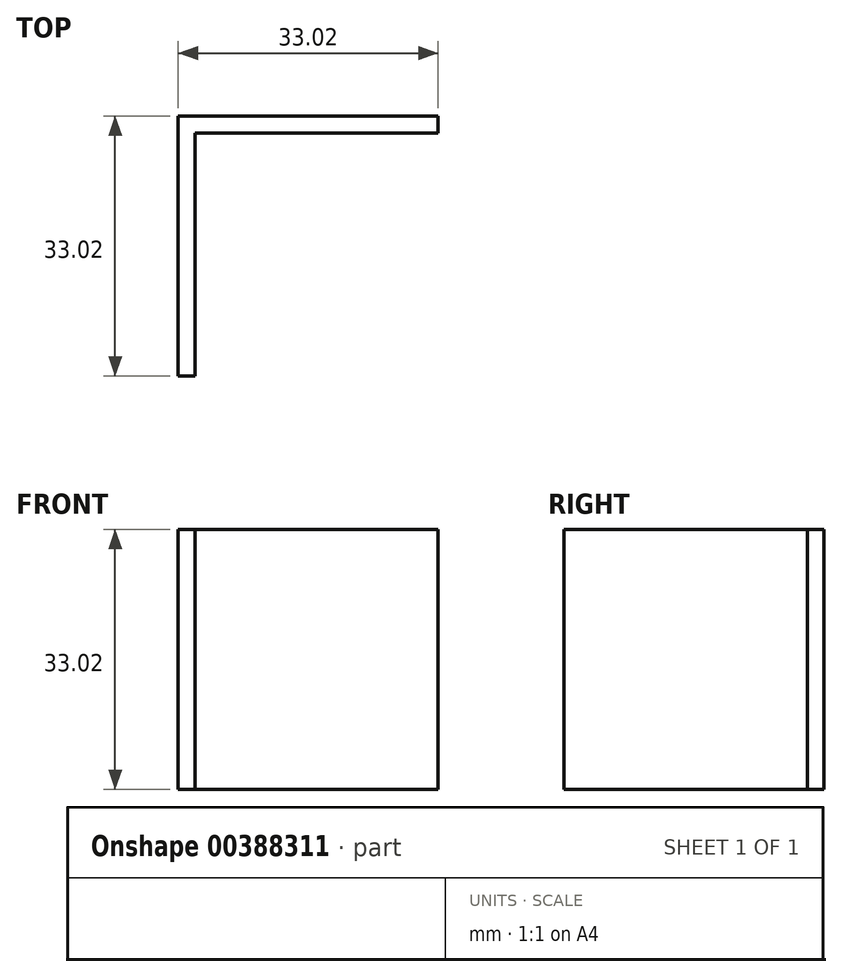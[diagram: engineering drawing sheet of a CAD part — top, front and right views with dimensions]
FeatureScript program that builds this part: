
annotation { "Feature Type Name" : "Feature", "Feature Type Description" : "" }
export const myFeature = defineFeature(function(context is Context, id is Id, definition is map)
    precondition{}
    {
        {
            var Q0;
            Q0=qCreatedBy(makeId("Front.planeOp"),FACE);
            var sketch = newSketch(context, id + "F0", { "sketchPlane" : qUnion([Q0])});
            skLineSegment(sketch, "E0", {"start": v(-20.89, 19.99) * mm, "end": v(-20.89, -13.03) * mm});
            skLineSegment(sketch, "E1", {"start": v(-20.89, -13.03) * mm, "end": v(12.13, -13.03) * mm});
            skLineSegment(sketch, "E2", {"start": v(12.13, -13.03) * mm, "end": v(12.13, 19.99) * mm});
            skLineSegment(sketch, "E3", {"start": v(12.13, 19.99) * mm, "end": v(-20.89, 19.99) * mm});
            skSolve(sketch);
        }
        {
            var Q0;
            Q0=makeQuery(id+"F0.imprint","IMPRINT",FACE,{"disambiguationData":[TD([[makeQuery(id+"F0.imprint","IMPRINT",EDGE,{"derivedFrom":sQuery(id+"F0.wireOp",EDGE,"E0")}),1.0]])]});
            extrude(context, id + "F1", {"entities" : qUnion([Q0]), "depth" : 33.02 * mm});
        }
        {
            var Q0;
            Q0=makeQuery(id+"F1.opExtrude","SWEPT_FACE",FACE,{"disambiguationData":[OSD([sQuery(id+"F0.wireOp",EDGE,"E1")])]});
            var Q1;
            Q1=makeQuery(id+"F1.opExtrude","SWEPT_FACE",FACE,{"disambiguationData":[OSD([sQuery(id+"F0.wireOp",EDGE,"E2")])]});
            var Q2;
            Q2=makeQuery(id+"F1.opExtrude","CAP_FACE",FACE,{"disambiguationData":[OSD([sQuery(id+"F0.wireOp",EDGE,"E0"),sQuery(id+"F0.wireOp",EDGE,"E1"),sQuery(id+"F0.wireOp",EDGE,"E2"),sQuery(id+"F0.wireOp",EDGE,"E3")])],"isStart":false});
            var Q3;
            Q3=makeQuery(id+"F1.opExtrude","SWEPT_FACE",FACE,{"disambiguationData":[OSD([sQuery(id+"F0.wireOp",EDGE,"E3")])]});
            shell(context, id + "F2", {"entities" : qUnion([Q0, Q1, Q2, Q3]), "thickness" : 2.13 * mm});
        }
    });
